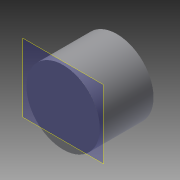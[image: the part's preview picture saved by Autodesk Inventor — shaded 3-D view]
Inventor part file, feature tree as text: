
AUTODESK INVENTOR PART (.ipt)
format: ipt  version: 2014 SP1 (Build 180222100, 222)  size: 75,264 bytes
history: native  units: in
note: dims shown in document units (in); Inventor stores cm internally (conversion verified against a paired STEP export)
features: plane x1, extrude x1, sketch x1, reference x1
ambient origin geometry x8: Origin, YZ Plane, XZ Plane, XY Plane, X Axis, Y Axis, Z Axis, Center Point
bodies: Solid1 (feature_tree)
feature tree (4):
  plane  "Work Plane1"
  extrude  "Extrusion1"  [1 undecoded]
  sketch  "Sketch1"  dims[d0=0.4331in d1=0.0in]
  reference  "Reference1"
note: 1 required parameter value undecoded (feature->parameter linkage not recoverable at this tier; creation-order binding heuristic only, values carry confidence <= 0.55)
